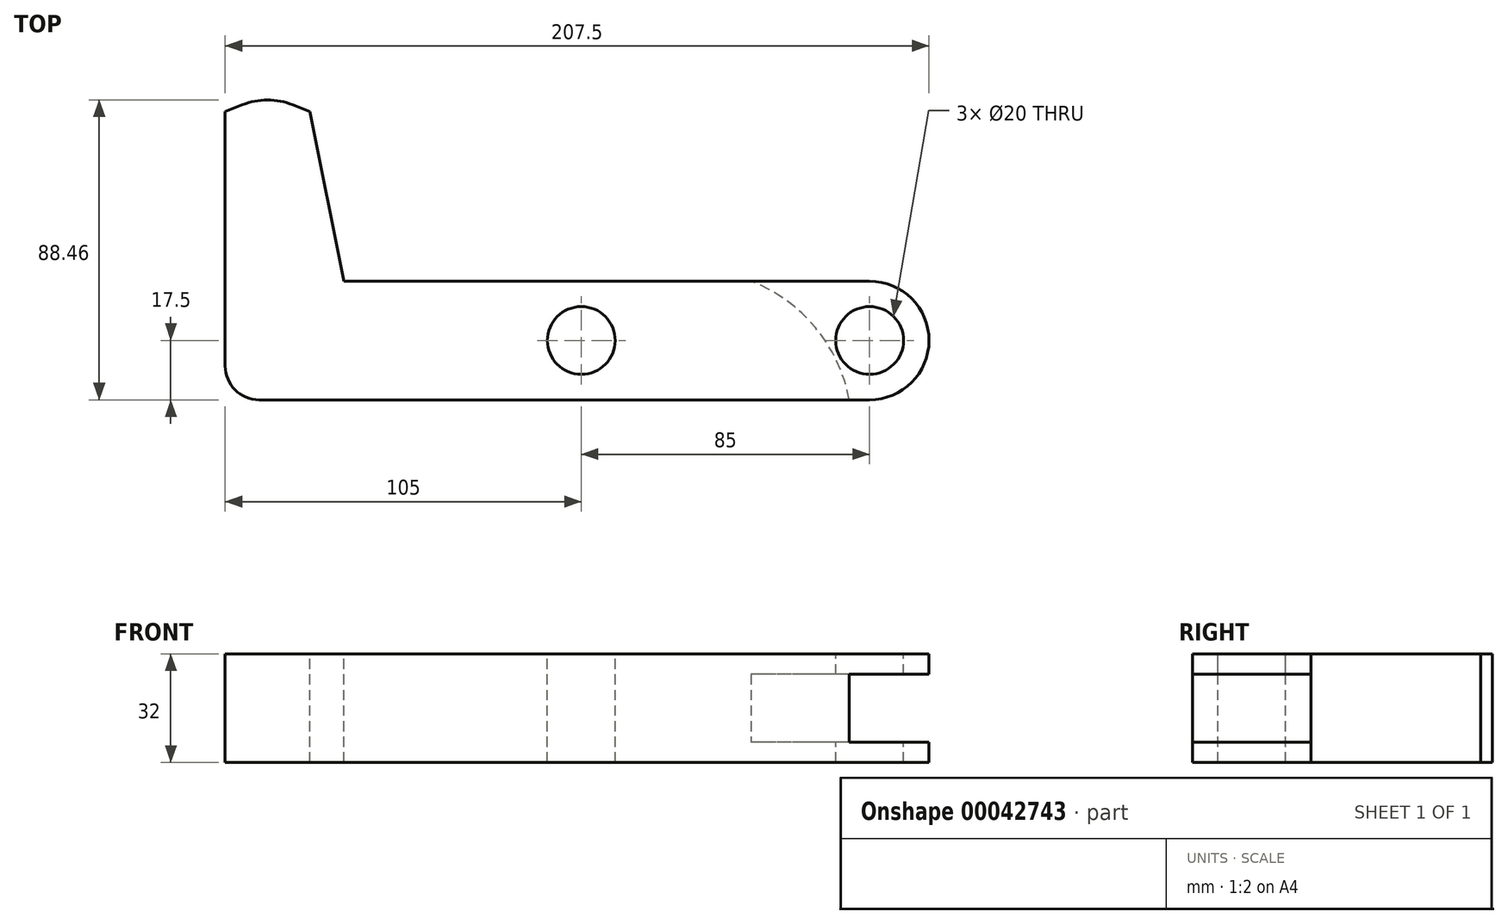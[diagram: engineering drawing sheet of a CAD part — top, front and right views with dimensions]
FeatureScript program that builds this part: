
annotation { "Feature Type Name" : "Feature", "Feature Type Description" : "" }
export const myFeature = defineFeature(function(context is Context, id is Id, definition is map)
    precondition{}
    {
        {
            var Q0;
            Q0=qCreatedBy(makeId("Top.planeOp"),FACE);
            var sketch = newSketch(context, id + "F0", { "sketchPlane" : qUnion([Q0])});
            skCircle(sketch, "E0", {"center": v(0, 0) * mm, "radius": 10 * mm});
            skArc(sketch, "E1", {"start": v(0, -17.5) * mm, "mid": v(17.5, 0) * mm, "end": v(0, 17.5) * mm});
            skLineSegment(sketch, "E2", {"start": v(0, 17.5) * mm, "end": v(-155, 17.5) * mm});
            skCircle(sketch, "E3", {"center": v(-85, 0) * mm, "radius": 10 * mm});
            skLineSegment(sketch, "E4", {"start": v(0, -17.5) * mm, "end": v(-180, -17.5) * mm});
            skLineSegment(sketch, "E5", {"start": v(-190, -7.5) * mm, "end": v(-190, 67.5) * mm});
            skLineSegment(sketch, "E6", {"start": v(-190, 67.5) * mm, "end": v(-165, 67.5) * mm});
            skLineSegment(sketch, "E7", {"start": v(-165, 67.5) * mm, "end": v(-155, 17.5) * mm});
            skPoint(sketch, "E8.visualSharp", {"position": v(-190, -17.5) * mm});
            skArc(sketch, "E8.filletArc", {"start": v(-190, -7.5) * mm, "mid": v(-187.07, -14.57) * mm, "end": v(-180, -17.5) * mm});
            skLineSegment(sketch, "E9", {"start": v(-190, 67.5) * mm, "end": v(-184.93, 69.53) * mm});
            skPoint(sketch, "E9.endSnap0", {"position": v(-177.5, 67.5) * mm});
            skLineSegment(sketch, "E10", {"start": v(-170.07, 69.53) * mm, "end": v(-165, 67.5) * mm});
            skPoint(sketch, "E11.visualSharp", {"position": v(-177.5, 72.5) * mm});
            skArc(sketch, "E11.filletArc", {"start": v(-170.07, 69.53) * mm, "mid": v(-177.5, 70.96) * mm, "end": v(-184.93, 69.53) * mm});
            skPoint(sketch, "E12", {"position": v(-35, 17.5) * mm});
            skPoint(sketch, "E13", {"position": v(-6, -17.5) * mm});
            skArc(sketch, "E14", {"start": v(-6, -17.5) * mm, "mid": v(-15.94, 3.78) * mm, "end": v(-35, 17.5) * mm});
            skSolve(sketch);
        }
        {
            var Q0;
            Q0 = qSketchRegion(id + "F0", true);
            extrude(context, id + "F1", {"entities" : qUnion([Q0]), "oppositeDirection" : true, "depth" : 6 * mm});
        }
        {
            var Q0;
            Q0 = qSketchRegion(id + "F0", true);
            extrude(context, id + "F2", {"entities" : qUnion([Q0]), "operationType" : NewBodyOperationType.ADD, "depth" : 26 * mm});
        }
        {
            var Q0;
            Q0=makeQuery(id+"F0.imprint","IMPRINT",FACE,{"disambiguationData":[TD([[makeQuery(id+"F0.imprint","IMPRINT",EDGE,{"derivedFrom":sQuery(id+"F0.wireOp",EDGE,"E0")}),-1.0]])]});
            extrude(context, id + "F3", {"entities" : qUnion([Q0]), "operationType" : NewBodyOperationType.REMOVE, "depth" : 20 * mm});
        }
    });
